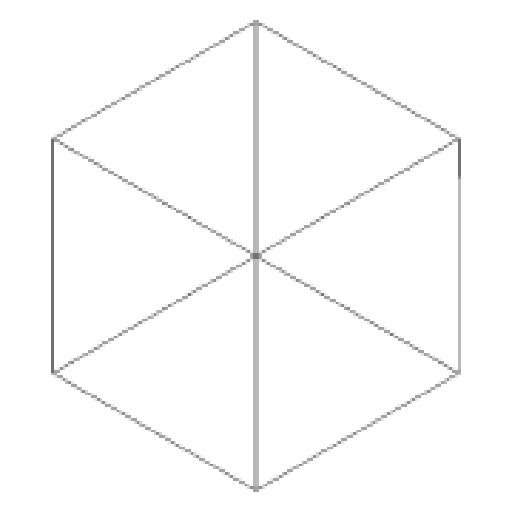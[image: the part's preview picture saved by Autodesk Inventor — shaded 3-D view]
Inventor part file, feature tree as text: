
AUTODESK INVENTOR PART (.ipt)
format: ipt  version: 2023 (Build 270158000, 158)  size: 157,696 bytes
history: native  units: in
note: dims shown in document units (in); Inventor stores cm internally (conversion verified against a paired STEP export)
features: extrude x4, sketch x4, projected_geometry x3, fillet x1
ambient origin geometry x8: Origin, YZ Plane, XZ Plane, XY Plane, X Axis, Y Axis, Z Axis, Center Point
bodies: Solid1 (feature_tree)
feature tree (12):
  extrude  "Extrusion1"  Depth=108.2677in TaperAngle=0.0deg
  extrude  "Extrusion2"  TaperAngle=0.0deg  [1 undecoded]
  extrude  "Extrusion3"  TaperAngle=0.0deg  [1 undecoded]
  extrude  "Extrusion4"  TaperAngle=0.0deg  [1 undecoded]
  fillet  "Fillet1"  Radius=0.25in
  sketch  "Sketch1"  dims[d0=108.2677in d2=108.2677in d3=0.0in]
  sketch  "Sketch2"  dims[d4=0.5in d5=0.0in d6=0.0in]
  projected_geometry  "Projected Loop1"
  sketch  "Sketch3"  dims[d7=0.5in d8=0.0in d9=0.0in]
  projected_geometry  "Projected Loop2"
  sketch  "Sketch4"  dims[d10=0.5in d11=0.0in d12=0.0in d13=0.25in]
  projected_geometry  "Projected Loop3"
note: 3 required parameter values undecoded (feature->parameter linkage not recoverable at this tier; creation-order binding heuristic only, values carry confidence <= 0.55)
